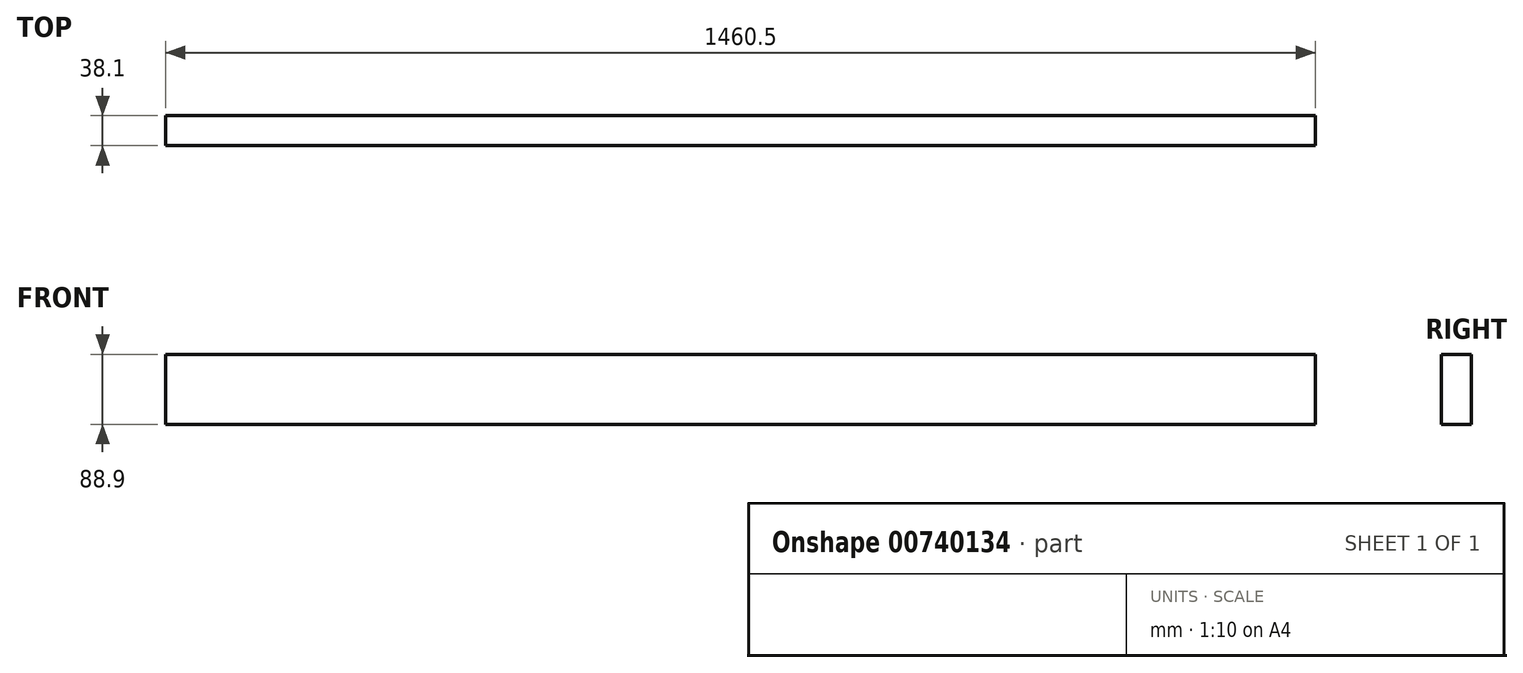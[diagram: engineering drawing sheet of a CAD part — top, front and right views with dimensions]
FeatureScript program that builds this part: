
annotation { "Feature Type Name" : "Feature", "Feature Type Description" : "" }
export const myFeature = defineFeature(function(context is Context, id is Id, definition is map)
    precondition{}
    {
        {
            var Q0;
            Q0=qCreatedBy(makeId("Right.planeOp"),FACE);
            var sketch = newSketch(context, id + "F0", { "sketchPlane" : qUnion([Q0])});
            skLineSegment(sketch, "E0.bottom", {"start": v(-79.68, 85.36) * mm, "end": v(-41.58, 85.36) * mm});
            skLineSegment(sketch, "E0.top", {"start": v(-79.68, -3.54) * mm, "end": v(-41.58, -3.54) * mm});
            skLineSegment(sketch, "E0.left", {"start": v(-79.68, 85.36) * mm, "end": v(-79.68, -3.54) * mm});
            skLineSegment(sketch, "E0.right", {"start": v(-41.58, 85.36) * mm, "end": v(-41.58, -3.54) * mm});
            skSolve(sketch);
        }
        {
            var Q0;
            Q0=makeQuery(id+"F0.imprint","IMPRINT",FACE,{"disambiguationData":[TD([[makeQuery(id+"F0.imprint","IMPRINT",EDGE,{"derivedFrom":sQuery(id+"F0.wireOp",EDGE,"E0.bottom")}),-1.0]])]});
            extrude(context, id + "F1", {"entities" : qUnion([Q0]), "depth" : 1371.6 * mm + 88.9 * mm, "offsetDistance" : 25.4 * mm});
        }
    });
